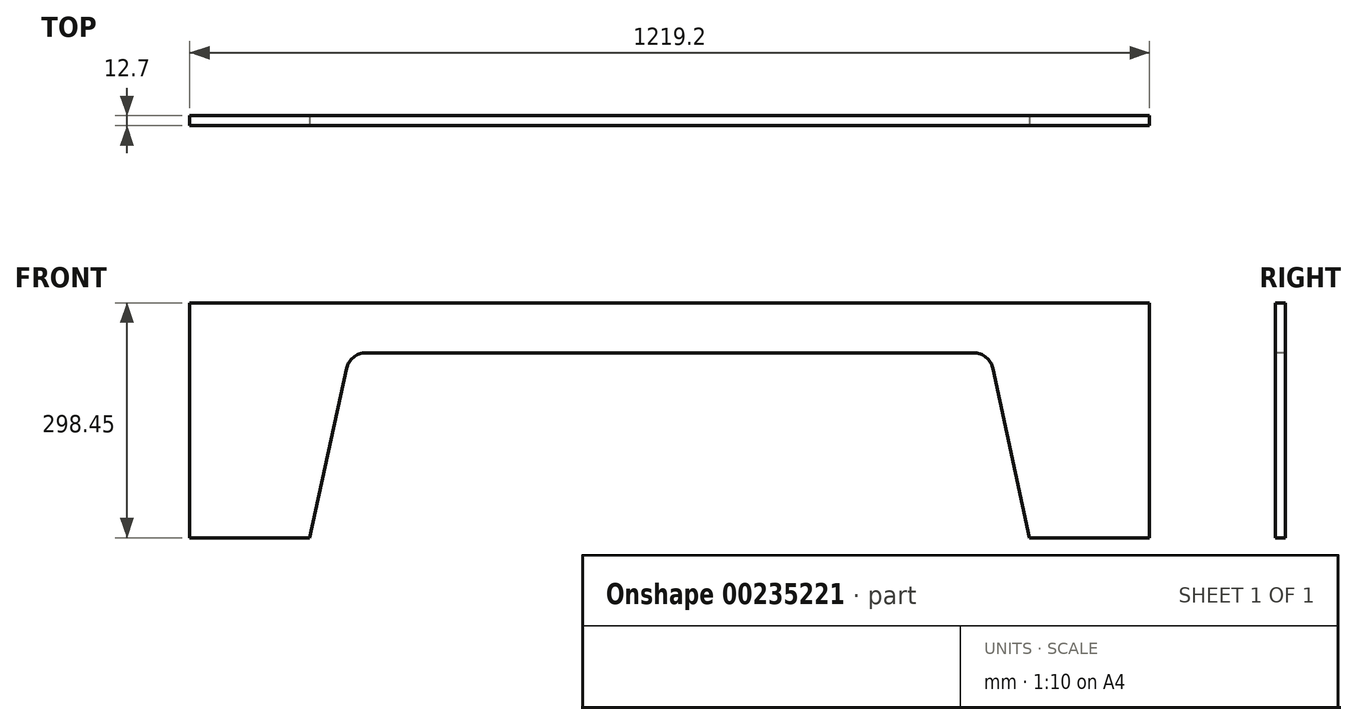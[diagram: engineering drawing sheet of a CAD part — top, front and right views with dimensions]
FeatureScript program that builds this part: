
annotation { "Feature Type Name" : "Feature", "Feature Type Description" : "" }
export const myFeature = defineFeature(function(context is Context, id is Id, definition is map)
    precondition{}
    {
        {
            var Q0;
            Q0=qCreatedBy(makeId("Front.planeOp"),FACE);
            var sketch = newSketch(context, id + "F0", { "sketchPlane" : qUnion([Q0])});
            skLineSegment(sketch, "E0.bottom", {"start": v(0, 0) * mm, "end": v(1219.2, 0) * mm});
            skLineSegment(sketch, "E0.top", {"start": v(0, 298.45) * mm, "end": v(1219.2, 298.45) * mm});
            skLineSegment(sketch, "E0.left", {"start": v(0, 0) * mm, "end": v(0, 298.45) * mm});
            skLineSegment(sketch, "E0.right", {"start": v(1219.2, 0) * mm, "end": v(1219.2, 298.45) * mm});
            skSolve(sketch);
        }
        {
            var Q0;
            Q0=makeQuery(id+"F0.imprint","IMPRINT",FACE,{"disambiguationData":[TD([[makeQuery(id+"F0.imprint","IMPRINT",EDGE,{"derivedFrom":sQuery(id+"F0.wireOp",EDGE,"E0.bottom")}),1.0]])]});
            extrude(context, id + "F1", {"entities" : qUnion([Q0]), "depth" : 12.7 * mm});
        }
        {
            var Q0;
            Q0=makeQuery(id+"F1.opExtrude","CAP_FACE",FACE,{"disambiguationData":[OSD([sQuery(id+"F0.wireOp",EDGE,"E0.bottom"),sQuery(id+"F0.wireOp",EDGE,"E0.top"),sQuery(id+"F0.wireOp",EDGE,"E0.left"),sQuery(id+"F0.wireOp",EDGE,"E0.right")])],"isStart":false});
            var sketch = newSketch(context, id + "F2", { "sketchPlane" : qUnion([Q0])});
            skLineSegment(sketch, "E1", {"start": v(152.4, 0) * mm, "end": v(198.87, 214.92) * mm});
            skLineSegment(sketch, "E2", {"start": v(223.7, 234.95) * mm, "end": v(995.5, 234.95) * mm});
            skLineSegment(sketch, "E3", {"start": v(1020.33, 214.92) * mm, "end": v(1066.8, 0) * mm});
            skLineSegment(sketch, "E4", {"start": v(1066.8, 0) * mm, "end": v(152.4, 0) * mm});
            skLineSegment(sketch, "E5", {"start": v(609.6, 298.45) * mm, "end": v(609.6, 0) * mm, "construction": true});
            skPoint(sketch, "E6.visualSharp", {"position": v(203.2, 234.95) * mm});
            skArc(sketch, "E6.filletArc", {"start": v(223.7, 234.95) * mm, "mid": v(207.74, 229.32) * mm, "end": v(198.87, 214.92) * mm});
            skPoint(sketch, "E7.visualSharp", {"position": v(1016, 234.95) * mm});
            skArc(sketch, "E7.filletArc", {"start": v(1020.33, 214.92) * mm, "mid": v(1011.46, 229.32) * mm, "end": v(995.5, 234.95) * mm});
            skSolve(sketch);
        }
        {
            var Q0;
            Q0=makeQuery(id+"F2.imprint","IMPRINT",FACE,{"disambiguationData":[TD([[makeQuery(id+"F2.imprint","IMPRINT",EDGE,{"derivedFrom":sQuery(id+"F2.wireOp",EDGE,"E1")}),-1.0]])]});
            extrude(context, id + "F3", {"entities" : qUnion([Q0]), "operationType" : NewBodyOperationType.REMOVE, "endBound" : BoundingType.THROUGH_ALL, "oppositeDirection" : true, "depth" : 25.4 * mm});
        }
    });
